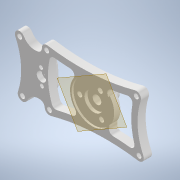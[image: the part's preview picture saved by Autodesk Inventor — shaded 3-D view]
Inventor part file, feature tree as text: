
AUTODESK INVENTOR PART (.ipt)
format: ipt  version: 2022 (Build 260153070, 153G)  size: 466,944 bytes
history: native  units: mm
features: reference x29, sketch x9, extrude x9, plane x6, other x6, projected_geometry x2
ambient origin geometry x8: Origin, YZ Plane, XZ Plane, XY Plane, X Axis, Y Axis, Z Axis, Center Point
bodies: Body1 (feature_tree)
feature tree (61):
  plane  "Work Plane1"
  sketch  "Sketch1"  dims[d0=1.0mm d1=10.0mm]
  plane  "Work Plane2"
  plane  "Work Plane3"
  extrude  "Extrusion2"  Depth=10.0mm
  extrude  "Extrusion3"  Depth=2.5mm
  extrude  "Extrusion4"  Depth=3.1mm
  sketch  "Sketch5"  dims[d9=1.5mm d12=57.25mm]
  plane  "Work Plane4"
  extrude  "Extrusion5"  Depth=57.25mm
  plane  "Work Plane5"
  extrude  "Extrusion6"  Depth=10.0mm TaperAngle=0.0deg
  extrude  "Extrusion7"  Depth=2.0mm TaperAngle=0.0deg
  extrude  "Extrusion8"  Depth=5.5mm
  extrude  "Extrusion9"  Depth=2.0mm
  sketch  "Sketch10"  dims[d25=3.0mm d26=2.0mm d27=0.0mm d28=10.0mm d29=0.0mm d30=0.15mm d31=1.25mm d32=10.0mm d33=0.0mm d34=4.0mm d35=4.0mm d36=4.0mm d37=6.125278mm d38=1.0mm d39=10.0mm d40=0.0mm d41=4.15mm d42=1.75mm d43=0.0mm d44=1.75mm d45=0.0mm]
  plane  "Work Plane6"
  extrude  "Extrusion10"  Depth=2.0mm TaperAngle=0.0deg
  reference  "Reference1"
  reference  "Reference2"
  reference  "Reference5"
  reference  "Reference6"
  reference  "Reference7"
  reference  "Reference8"
  reference  "Reference9"
  reference  "Reference10"
  reference  "Reference11"
  reference  "Reference12"
  reference  "Reference13"
  reference  "Reference14"
  reference  "Reference15"
  reference  "Reference16"
  reference  "Reference17"
  reference  "Reference18"
  reference  "Reference19"
  reference  "Reference20"
  reference  "Reference21"
  reference  "Reference22"
  sketch  "Sketch3"  dims[d2=2.5mm d3=2.5mm]
  reference  "Reference27"
  reference  "Reference29"
  reference  "Reference30"
  reference  "Reference32"
  projected_geometry  "Projected Loop3"
  sketch  "Sketch4"  dims[d4=3.1mm d5=3.1mm]
  projected_geometry  "Projected Loop4"
  sketch  "Sketch6"  dims[d13=3.05mm d14=10.0mm d15=0.0mm]
  reference  "Reference33"
  sketch  "Sketch7"  dims[d17=0.25mm d18=2.0mm d19=0.0mm]
  sketch  "Sketch8"  dims[d20=3.5mm d21=5.5mm]
  sketch  "Sketch9"  dims[d22=2.0mm d23=0.0mm d24=18.0mm]
  reference  "Reference34"
  reference  "Reference35"
  reference  "Reference36"
  reference  "Reference37"
  other  "<userpath> laptop\Desktop\SumoBot\sumobotLIDAR\AssemblyV3.iam"
  other  "AssemblyV3.iam"
  other  "SRM-12-06A:1"
  other  "MOTOR:1"
  other  "AS5600_mount:1"
  other  "608ZZ bearing:1"
